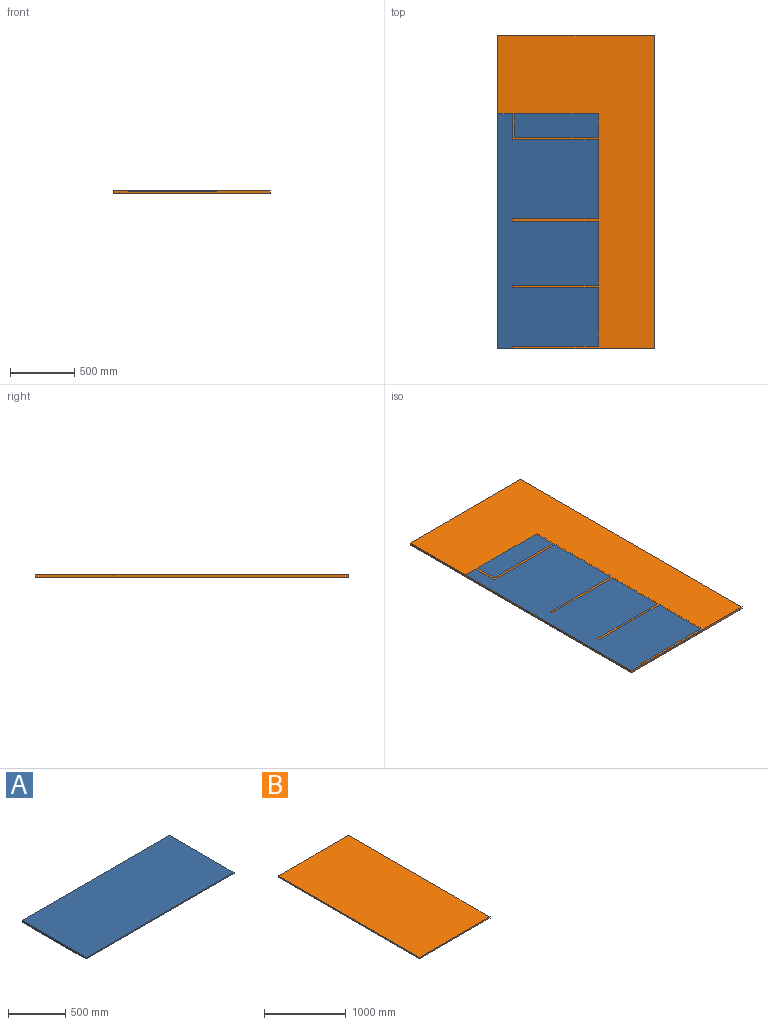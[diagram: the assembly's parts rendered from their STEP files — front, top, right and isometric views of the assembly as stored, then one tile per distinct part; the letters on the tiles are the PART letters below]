
ASSEMBLY  parts=2 mates=1
PART A: 24 faces, bbox 1828.8x800.1x18.3 mm
  f0: plane 1828.8x11.91mm, normal (0,-1,0), area 21774.2mm2, adj f1,f4,f6,f23
  f1: plane 800.1x18.26mm, normal (-1,0,0), area 14375mm2, adj f0,f2,f3,f5,f6,f7,f9,f10
  f2: plane 649.29x184.94mm, normal (0,0,-1), area 120081.7mm2, adj f1,f7,f8,f9
  f3: plane 1828.8x781.84mm, normal (0,0,-1), area 1257630.4mm2, adj f1,f4,f5,f10,f11,f12,f13,f14
  f4: plane 800.1x18.26mm, normal (1,0,0), area 10252mm2, adj f0,f3,f5,f6,f22,f23
  f5: plane 1828.8x18.26mm, normal (0,1,0), area 33387mm2, adj f1,f3,f4,f6
  f6: plane 1828.8x800.1mm, normal (0,0,1), area 1463222.9mm2, adj f0,f1,f4,f5
  f7: plane 184.94x6.35mm, normal (0,-1,0), area 1174.4mm2, adj f1,f2,f8,f23
  f8: plane 649.29x6.35mm, normal (1,0,0), area 4123mm2, adj f2,f7,f9,f23
  f9: plane 184.94x6.35mm, normal (0,1,0), area 1174.4mm2, adj f1,f2,f8,f23
  f10: plane 203.2x6.35mm, normal (0,-1,0), area 1290.3mm2, adj f1,f3,f11,f23
  f11: plane 667.54x6.35mm, normal (-1,0,0), area 4238.9mm2, adj f3,f10,f12,f23
  f12: plane 616.74x6.35mm, normal (0,-1,0), area 3916.3mm2, adj f3,f11,f13,f23
  f13: plane 667.54x6.35mm, normal (1,0,0), area 4238.9mm2, adj f3,f12,f14,f23
  f14: plane 18.26x6.35mm, normal (0,-1,0), area 115.9mm2, adj f3,f13,f15,f23
  f15: plane 667.54x6.35mm, normal (-1,0,0), area 4238.9mm2, adj f3,f14,f16,f23
  f16: plane 496.09x6.35mm, normal (0,-1,0), area 3150.2mm2, adj f3,f15,f17,f23
  f17: plane 667.54x6.35mm, normal (1,0,0), area 4238.9mm2, adj f3,f16,f18,f23
  f18: plane 18.26x6.35mm, normal (0,-1,0), area 115.9mm2, adj f3,f17,f19,f23
  f19: plane 667.54x6.35mm, normal (-1,0,0), area 4238.9mm2, adj f3,f18,f20,f23
  f20: plane 457.99x6.35mm, normal (0,-1,0), area 2908.3mm2, adj f3,f19,f21,f23
  f21: plane 667.54x6.35mm, normal (1,0,0), area 4238.9mm2, adj f3,f20,f22,f23
  f22: plane 18.26x6.35mm, normal (0,-1,0), area 115.9mm2, adj f3,f4,f21,f23
  f23: plane 1828.8x685.8mm, normal (0,0,-1), area 85510.8mm2, adj f0,f1,f4,f7,f8,f9,f10,f11
PART B: 6 faces, bbox 1219.2x2438.4x18.3 mm
  f0: plane 2438.4x18.26mm, normal (1,0,0), area 44516mm2, adj f1,f3,f4,f5
  f1: plane 1219.2x18.26mm, normal (0,1,0), area 22258mm2, adj f0,f2,f4,f5
  f2: plane 2438.4x18.26mm, normal (-1,0,0), area 44516mm2, adj f1,f3,f4,f5
  f3: plane 1219.2x18.26mm, normal (0,-1,0), area 22258mm2, adj f0,f2,f4,f5
  f4: plane 2438.4x1219.2mm, normal (0,0,1), area 2972897.3mm2, adj f0,f1,f2,f3
  f5: plane 2438.4x1219.2mm, normal (0,0,-1), area 2972897.3mm2, adj f0,f1,f2,f3
PLACE A rot(axis=(-0.71,0.71,0),180deg) t=(457.2,914.4,850.9)mm
PLACE B t=(1219.2,0,0)mm
MATE fastened A.f6 <-> B.f5  axis (0,0,-1) through (0,0,0)mm
